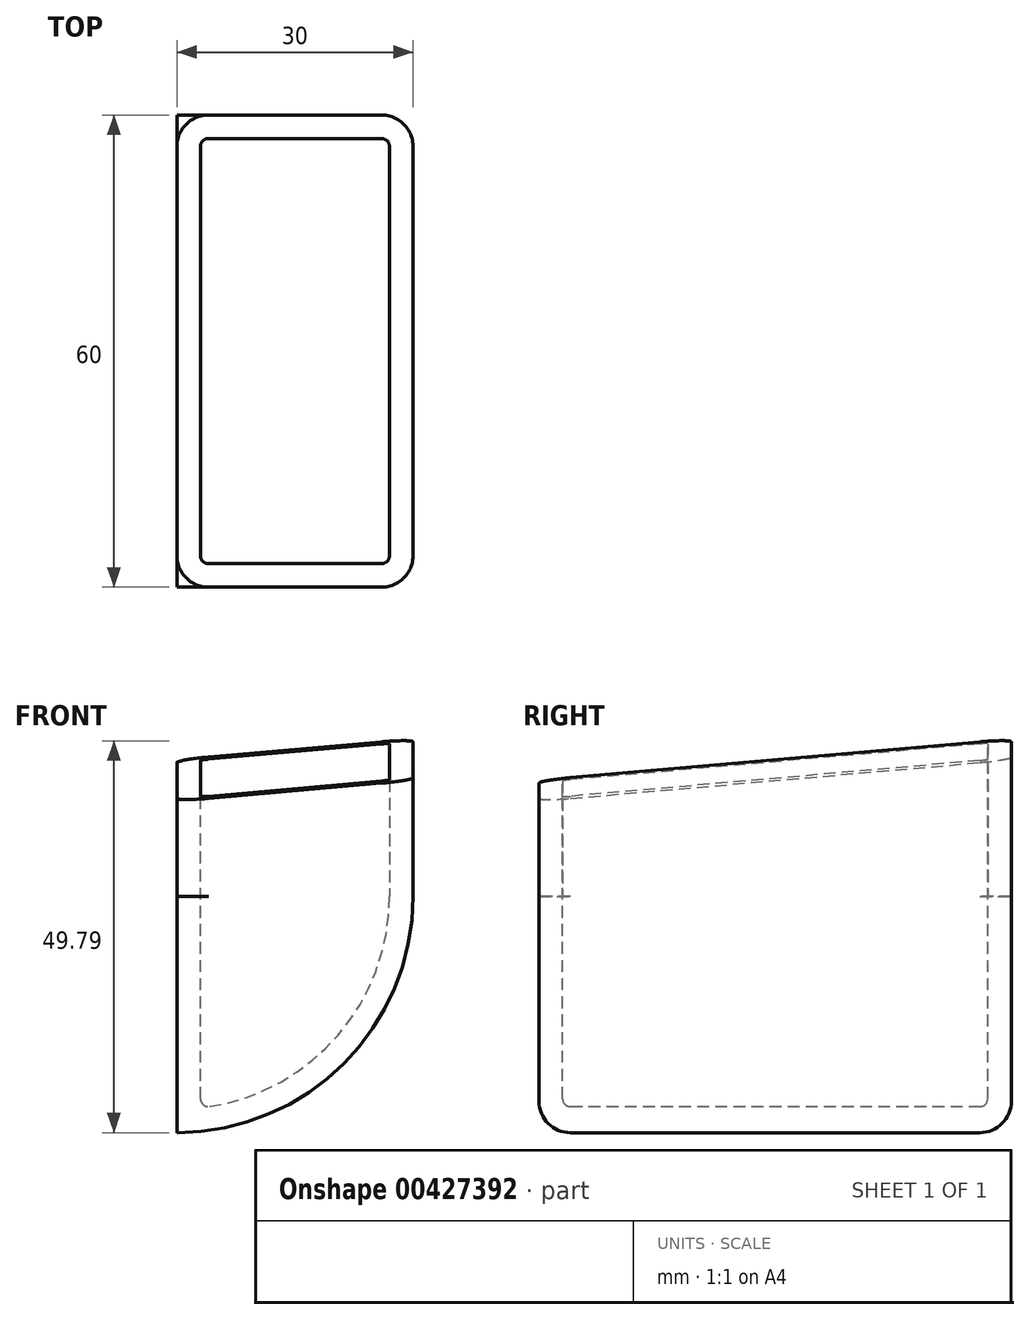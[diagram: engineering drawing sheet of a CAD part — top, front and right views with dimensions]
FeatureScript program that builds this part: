
annotation { "Feature Type Name" : "Feature", "Feature Type Description" : "" }
export const myFeature = defineFeature(function(context is Context, id is Id, definition is map)
    precondition{}
    {
        {
            var Q0;
            Q0=qCreatedBy(makeId("Front.planeOp"),FACE);
            var sketch = newSketch(context, id + "F0", { "sketchPlane" : qUnion([Q0])});
            skArc(sketch, "E0", {"start": v(0, -30) * mm, "mid": v(21.21, -21.21) * mm, "end": v(30, 0) * mm});
            skLineSegment(sketch, "E1", {"start": v(0, -30) * mm, "end": v(0, 0) * mm});
            skLineSegment(sketch, "E2", {"start": v(30, 0) * mm, "end": v(0, 0) * mm});
            skPoint(sketch, "E3.orphan", {"position": v(34.48, 0) * mm});
            skPoint(sketch, "E4.orphan", {"position": v(0, -36.55) * mm});
            skSolve(sketch);
        }
        {
            var Q0;
            Q0=makeQuery(id+"F0.imprint","IMPRINT",FACE,{"disambiguationData":[TD([[makeQuery(id+"F0.imprint","IMPRINT",EDGE,{"derivedFrom":sQuery(id+"F0.wireOp",EDGE,"E0")}),1.0]])]});
            extrude(context, id + "F1", {"entities" : qUnion([Q0]), "endBound" : BoundingType.SYMMETRIC, "depth" : 60 * mm});
        }
        {
            var Q0;
            Q0=makeQuery(id+"F1.opExtrude","SWEPT_FACE",FACE,{"disambiguationData":[OSD([sQuery(id+"F0.wireOp",EDGE,"E2")])]});
            shell(context, id + "F2", {"entities" : qUnion([Q0]), "thickness" : 3 * mm});
        }
        {
            var Q0;
            {var subQ0=sQuery(id+"F0.wireOp",EDGE,"E0");Q0=makeQuery(id+"F2.opShell","OFFSET_EDGE",EDGE,{"disambiguationData":[OSD([subQ0]),TDD([makeQuery(id+"F1.opExtrude","CAP_EDGE",EDGE,{"disambiguationData":[OSD([subQ0])],"isStart":false})])]});}
            var Q1;
            {var subQ0=sQuery(id+"F0.wireOp",EDGE,"E0");Q1=makeQuery(id+"F2.opShell","OFFSET_EDGE",EDGE,{"disambiguationData":[OSD([subQ0]),TDD([makeQuery(id+"F1.opExtrude","CAP_EDGE",EDGE,{"disambiguationData":[OSD([subQ0])],"isStart":true})])]});}
            fillet(context, id + "F3", {"entities" : qUnion([Q0, Q1]), "radius" : 1 * mm, "tangentPropagation" : true, "allowEdgeOverflow" : false});
        }
        {
            var Q0;
            Q0=makeQuery(id+"F1.opExtrude","CAP_EDGE",EDGE,{"disambiguationData":[OSD([sQuery(id+"F0.wireOp",EDGE,"E0")])],"isStart":false});
            var Q1;
            Q1=makeQuery(id+"F1.opExtrude","CAP_EDGE",EDGE,{"disambiguationData":[OSD([sQuery(id+"F0.wireOp",EDGE,"E0")])],"isStart":true});
            fillet(context, id + "F4", {"entities" : qUnion([Q0, Q1]), "radius" : 4 * mm, "tangentPropagation" : true, "allowEdgeOverflow" : false});
        }
        {
            var Q0;
            Q0=makeQuery(id+"F1.opExtrude","SWEPT_FACE",FACE,{"disambiguationData":[OSD([sQuery(id+"F0.wireOp",EDGE,"E2")])]});
            var sketch = newSketch(context, id + "F5", { "sketchPlane" : qUnion([Q0])});
            skLineSegment(sketch, "E5.0", {"start": v(26, -30) * mm, "end": v(0, -30) * mm});
            skPoint(sketch, "E6.0", {"position": v(28.83, -28.83) * mm});
            skArc(sketch, "E7.0", {"start": v(27, -26) * mm, "mid": v(26.7, -26.7) * mm, "end": v(26, -27) * mm});
            skLineSegment(sketch, "E8.0", {"start": v(26, -27) * mm, "end": v(3, -27) * mm});
            skArc(sketch, "E9.0", {"start": v(26, -30) * mm, "mid": v(28.83, -28.83) * mm, "end": v(30, -26) * mm});
            skLineSegment(sketch, "E10.0", {"start": v(30, -26) * mm, "end": v(30, 26) * mm});
            skLineSegment(sketch, "E11.0", {"start": v(27, -26) * mm, "end": v(27, 26) * mm});
            skLineSegment(sketch, "E12.0", {"start": v(3, -27) * mm, "end": v(3, 27) * mm});
            skLineSegment(sketch, "E13.0", {"start": v(0, -30) * mm, "end": v(0, 30) * mm});
            skLineSegment(sketch, "E14.0", {"start": v(26, 30) * mm, "end": v(0, 30) * mm});
            skLineSegment(sketch, "E15.0", {"start": v(26, 27) * mm, "end": v(3, 27) * mm});
            skArc(sketch, "E16.0", {"start": v(26, 27) * mm, "mid": v(26.7, 26.7) * mm, "end": v(27, 26) * mm});
            skArc(sketch, "E17.0", {"start": v(30, 26) * mm, "mid": v(28.83, 28.83) * mm, "end": v(26, 30) * mm});
            skSolve(sketch);
        }
        {
            var Q0;
            Q0=makeQuery(id+"F5.imprint","IMPRINT",FACE,{"disambiguationData":[TD([[makeQuery(id+"F5.imprint","IMPRINT",EDGE,{"derivedFrom":sQuery(id+"F5.wireOp",EDGE,"E5.0")}),-1.0]])]});
            extrude(context, id + "F6", {"entities" : qUnion([Q0]), "operationType" : NewBodyOperationType.ADD, "depth" : 20 * mm});
        }
        {
            var Q0;
            Q0=makeQuery(id+"F6.boolean.opBoolean","MERGE",FACE,{"derivedFrom":[makeQuery(id+"F1.opExtrude","SWEPT_FACE",FACE,{"disambiguationData":[OSD([sQuery(id+"F0.wireOp",EDGE,"E1")])]}),makeQuery(id+"F6.opExtrude","SWEPT_FACE",FACE,{"disambiguationData":[OSD([sQuery(id+"F5.wireOp",EDGE,"E13.0")])]})]});
            var sketch = newSketch(context, id + "F7", { "sketchPlane" : qUnion([Q0])});
            skLineSegment(sketch, "E18.0", {"start": v(30, 20) * mm, "end": v(-30, 20) * mm});
            skLineSegment(sketch, "E19", {"start": v(30, 20) * mm, "end": v(30, 14.75) * mm});
            skLineSegment(sketch, "E20", {"start": v(30, 14.75) * mm, "end": v(-30, 20) * mm});
            skSolve(sketch);
        }
        {
            var Q0;
            Q0=makeQuery(id+"F7.imprint","IMPRINT",FACE,{"disambiguationData":[TD([[makeQuery(id+"F7.imprint","IMPRINT",EDGE,{"derivedFrom":sQuery(id+"F7.wireOp",EDGE,"E18.0")}),1.0]])]});
            extrude(context, id + "F8", {"entities" : qUnion([Q0]), "operationType" : NewBodyOperationType.REMOVE, "oppositeDirection" : true, "depth" : 40 * mm});
        }
        {
            var Q0;
            {var subQ0=sQuery(id+"F5.wireOp",EDGE,"E14.0");Q0=makeQuery(id+"F8.boolean.opBoolean","MERGE",EDGE,{"derivedFrom":[makeQuery(id+"F6.opExtrude","CAP_EDGE",EDGE,{"disambiguationData":[OSD([subQ0])],"isStart":false}),makeQuery(id+"F8.opExtrude","SWEPT_EDGE",EDGE,{"disambiguationData":[OSD([sQuery(id+"F0.wireOp",EDGE,"E1"),sQuery(id+"F5.wireOp",EDGE,"E13.0"),subQ0,sQuery(id+"F7.wireOp",EDGE,"E18.0"),sQuery(id+"F7.wireOp",EDGE,"E20")])]})]});}
            cPlane(context, id + "F9", {"entities" : qUnion([Q0]), "cplaneType" : CPlaneType.LINE_ANGLE, "offset" : 25 * mm, "angle" : 5 * degree, "oppositeDirection" : true, "width" : 150 * mm, "height" : 150 * mm});
        }
        {
            var Q0;
            Q0=qCreatedBy(id+"F9.planeOp",FACE);
            var sketch = newSketch(context, id + "F10", { "sketchPlane" : qUnion([Q0])});
            skLineSegment(sketch, "E21.0", {"start": v(30, 17.3) * mm, "end": v(26, 17.3) * mm});
            skLineSegment(sketch, "E22.0", {"start": v(26, 17.3) * mm, "end": v(0, 17.3) * mm});
            skLineSegment(sketch, "E23", {"start": v(30, 17.3) * mm, "end": v(0, 14.68) * mm});
            skLineSegment(sketch, "E24.0", {"start": v(0, 14.68) * mm, "end": v(0, 17.3) * mm});
            skPoint(sketch, "E25.orphan", {"position": v(0, -28.52) * mm});
            skSolve(sketch);
        }
        {
            var Q0;
            Q0=makeQuery(id+"F10.imprint","IMPRINT",FACE,{"disambiguationData":[TD([[makeQuery(id+"F10.imprint","IMPRINT",EDGE,{"derivedFrom":sQuery(id+"F10.wireOp",EDGE,"E21.0")}),1.0]])]});
            extrude(context, id + "F11", {"entities" : qUnion([Q0]), "operationType" : NewBodyOperationType.REMOVE, "depth" : 100 * mm});
        }
        {
            var Q0;
            Q0=qCreatedBy(makeId("Top.planeOp"),FACE);
            cPlane(context, id + "F12", {"entities" : qUnion([Q0]), "cplaneType" : CPlaneType.OFFSET, "offset" : 25 * mm, "width" : 150 * mm, "height" : 150 * mm});
        }
        {
            var Q0;
            {var subQ0=sQuery(id+"F0.wireOp",EDGE,"E1");Q0=makeQuery(id+"F6.boolean.opBoolean","MERGE",EDGE,{"derivedFrom":[makeQuery(id+"F2.opShell","OFFSET_EDGE",EDGE,{"disambiguationData":[OSD([subQ0]),TDD([makeQuery(id+"F1.opExtrude","CAP_EDGE",EDGE,{"disambiguationData":[OSD([subQ0])],"isStart":true})])]}),makeQuery(id+"F6.opExtrude","SWEPT_EDGE",EDGE,{"disambiguationData":[OSD([sQuery(id+"F5.wireOp",EDGE,"E12.0"),sQuery(id+"F5.wireOp",EDGE,"E15.0")])]})]});}
            fillet(context, id + "F13", {"entities" : qUnion([Q0]), "radius" : 1 * mm, "tangentPropagation" : true, "allowEdgeOverflow" : false});
        }
        {
            var Q0;
            Q0=qCreatedBy(id+"F12.planeOp",FACE);
            var sketch = newSketch(context, id + "F14", { "sketchPlane" : qUnion([Q0])});
            skLineSegment(sketch, "E26.0", {"start": v(0, 30) * mm, "end": v(4, 30) * mm});
            skLineSegment(sketch, "E27.0", {"start": v(0, 26) * mm, "end": v(0, 30) * mm});
            skLineSegment(sketch, "E28.0", {"start": v(0, -30) * mm, "end": v(4, -30) * mm});
            skArc(sketch, "E29", {"start": v(4, 30) * mm, "mid": v(1.17, 28.83) * mm, "end": v(0, 26) * mm});
            skLineSegment(sketch, "E30.0", {"start": v(0, -30) * mm, "end": v(0, -26) * mm});
            skArc(sketch, "E31", {"start": v(0, -26) * mm, "mid": v(1.17, -28.83) * mm, "end": v(4, -30) * mm});
            skPoint(sketch, "E32.orphan", {"position": v(26, 30) * mm});
            skPoint(sketch, "E33.orphan", {"position": v(26, -30) * mm});
            skSolve(sketch);
        }
        {
            var Q0;
            Q0 = qSketchRegion(id + "F14", true);
            extrude(context, id + "F15", {"entities" : qUnion([Q0]), "operationType" : NewBodyOperationType.REMOVE, "oppositeDirection" : true, "depth" : 25 * mm});
        }
    });
